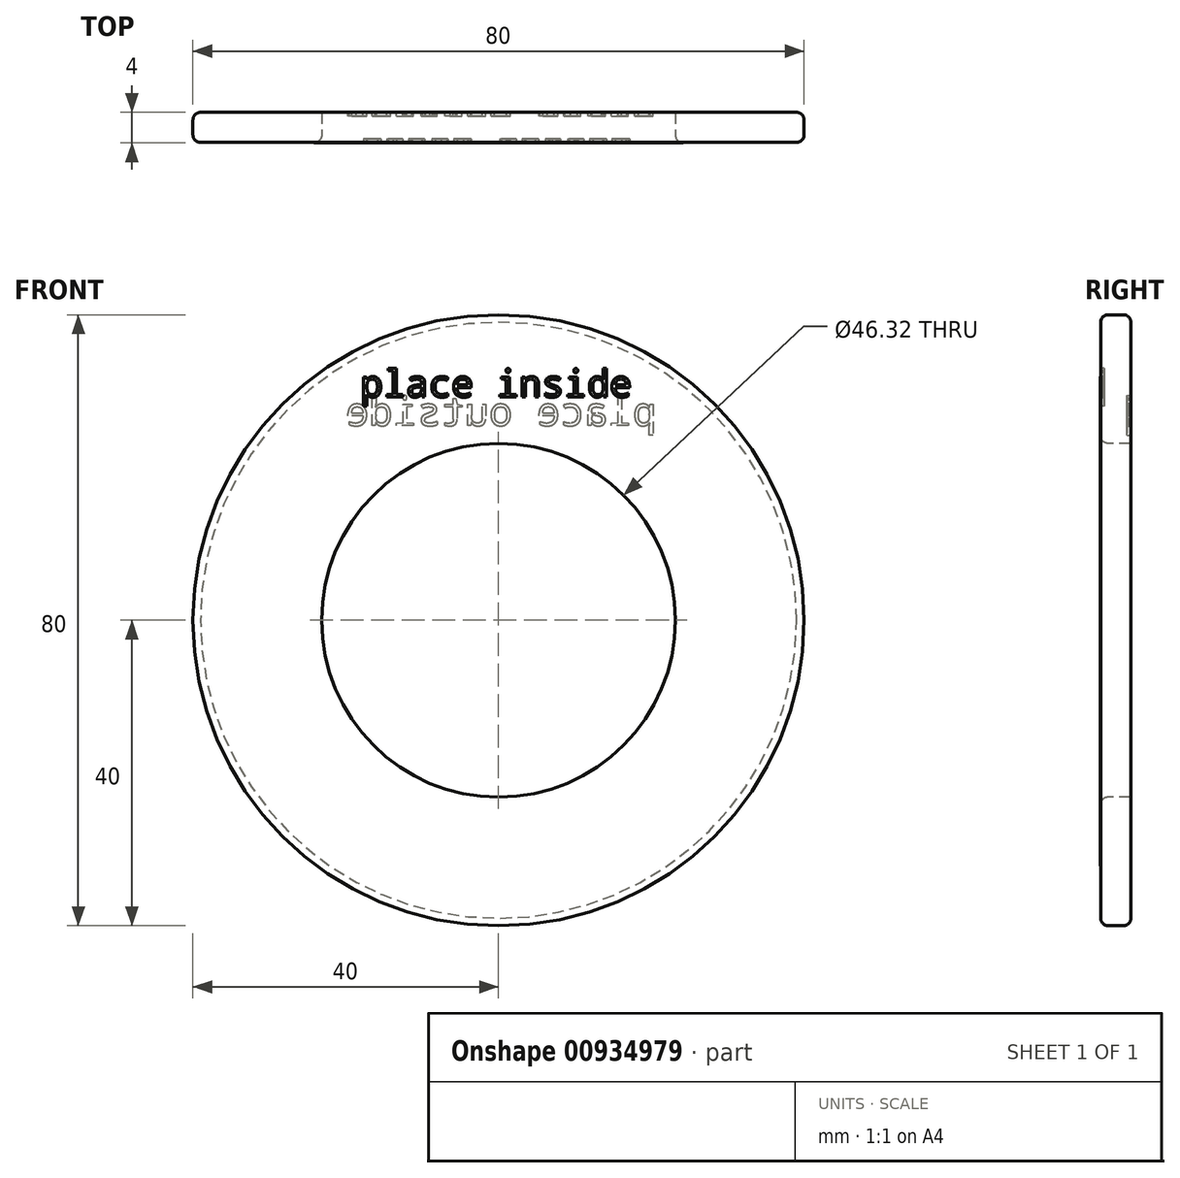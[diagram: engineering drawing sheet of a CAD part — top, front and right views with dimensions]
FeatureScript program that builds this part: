
annotation { "Feature Type Name" : "Feature", "Feature Type Description" : "" }
export const myFeature = defineFeature(function(context is Context, id is Id, definition is map)
    precondition{}
    {
        {
            var Q0;
            Q0=qCreatedBy(makeId("Right.planeOp"),FACE);
            var sketch = newSketch(context, id + "F0", { "sketchPlane" : qUnion([Q0])});
            skLineSegment(sketch, "E0", {"start": v(0, 0) * mm, "end": v(73, 0) * mm, "construction": true});
            skLineSegment(sketch, "E1.bottom", {"start": v(73, 0) * mm, "end": v(69, 0) * mm});
            skPoint(sketch, "E2.orphan", {"position": v(0, 16.15) * mm});
            skLineSegment(sketch, "E3.0", {"start": v(69, 16.15) * mm, "end": v(69, 16.15) * mm});
            skLineSegment(sketch, "E4.0", {"start": v(69, 23.16) * mm, "end": v(73, 23.16) * mm});
            skLineSegment(sketch, "E5", {"start": v(72, 40) * mm, "end": v(70.05, 40) * mm});
            skLineSegment(sketch, "E6", {"start": v(69.05, 39) * mm, "end": v(69, 23.16) * mm});
            skPoint(sketch, "E7.visualSharp", {"position": v(69.05, 40) * mm});
            skArc(sketch, "E7.filletArc", {"start": v(70.05, 40) * mm, "mid": v(69.34, 39.7) * mm, "end": v(69.05, 39) * mm});
            skPoint(sketch, "E8.visualSharp", {"position": v(73, 40) * mm});
            skArc(sketch, "E8.filletArc", {"start": v(73, 39.01) * mm, "mid": v(72.7, 39.71) * mm, "end": v(72, 40) * mm});
            skLineSegment(sketch, "E9", {"start": v(73, 39.01) * mm, "end": v(73, 23.16) * mm});
            skSolve(sketch);
        }
        {
            var Q0;
            Q0=makeQuery(id+"F0.imprint","IMPRINT",FACE,{"disambiguationData":[TD([[makeQuery(id+"F0.imprint","IMPRINT",EDGE,{"derivedFrom":sQuery(id+"F0.wireOp",EDGE,"E4.0")}),1.0]])]});
            var Q1;
            Q1=sQuery(id+"F0.wireOp",EDGE,"E0");
            revolve(context, id + "F1", {"surfaceOperationType" : NewSurfaceOperationType.NEW, "entities" : qUnion([Q0]), "axis" : qUnion([Q1]), "revolveType" : RevolveType.FULL});
        }
        {
            var Q0;
            Q0=makeQuery(id+"F1.opRevolve","SWEPT_EDGE",EDGE,{"disambiguationData":[OSD([sQuery(id+"F0.wireOp",EDGE,"E4.0"),sQuery(id+"F0.wireOp",EDGE,"E6")])]});
            fillet(context, id + "F2", {"entities" : qUnion([Q0]), "radius" : 1 * mm, "tangentPropagation" : true, "allowEdgeOverflow" : false});
        }
        {
            var Q0;
            Q0=qCreatedBy(makeId("Front.planeOp"),FACE);
            var sketch = newSketch(context, id + "F3", { "sketchPlane" : qUnion([Q0])});
            skText(sketch, "E10", { "text": "place inside", "fontName": "DroidSansMono.ttf"});
            const initialGuessF3  = {"E10": [-0.01804, 0.02923, 1, 0, 0.00355]};
            skSetInitialGuess(sketch, initialGuessF3);
            skSolve(sketch);
        }
        {
            var Q0;
            Q0 = qSketchRegion(id + "F3", true);
            extrude(context, id + "F4", {"entities" : qUnion([Q0]), "operationType" : NewBodyOperationType.REMOVE, "endBound" : BoundingType.UP_TO_NEXT, "oppositeDirection" : true, "depth" : 66.4 * mm, "hasOffset" : true, "offsetDistance" : 0.5 * mm, "offsetOppositeDirection" : true, "hasSecondDirection" : true, "secondDirectionBound" : SecondDirectionBoundingType.UP_TO_NEXT, "secondDirectionOppositeDirection" : true, "secondDirectionDepth" : 41.3 * mm});
        }
        {
            var Q0;
            Q0=qCreatedBy(makeId("Front.planeOp"),FACE);
            cPlane(context, id + "F5", {"entities" : qUnion([Q0]), "cplaneType" : CPlaneType.OFFSET, "offset" : 97.9 * mm, "oppositeDirection" : true, "width" : 150 * mm, "height" : 150 * mm});
        }
        {
            var Q0;
            Q0=qCreatedBy(id+"F5.planeOp",FACE);
            var sketch = newSketch(context, id + "F6", { "sketchPlane" : qUnion([Q0])});
            skLineSegment(sketch, "E11", {"start": v(77.57, 0) * mm, "end": v(-72.43, 0) * mm, "construction": true});
            skLineSegment(sketch, "E12", {"start": v(0, 70.28) * mm, "end": v(0, -87.63) * mm, "construction": true});
            skSolve(sketch);
        }
        {
            var Q0;
            Q0=sQuery(id+"F6.wireOp",EDGE,"E12");
            cPlane(context, id + "F7", {"entities" : qUnion([Q0]), "cplaneType" : CPlaneType.LINE_ANGLE, "offset" : 25 * mm, "angle" : 90 * degree, "width" : 150 * mm, "height" : 150 * mm});
        }
        {
            var Q0;
            Q0=qCreatedBy(id+"F7.planeOp",FACE);
            var sketch = newSketch(context, id + "F8", { "sketchPlane" : qUnion([Q0])});
            skText(sketch, "E13", { "text": "place outside", "fontName": "DroidSansMono.ttf"});
            const initialGuessF8  = {"E13": [-0.0206, 0.02548, 1, 0, 0.00375]};
            skSetInitialGuess(sketch, initialGuessF8);
            skSolve(sketch);
        }
        {
            var Q0;
            Q0 = qSketchRegion(id + "F8", true);
            extrude(context, id + "F9", {"entities" : qUnion([Q0]), "operationType" : NewBodyOperationType.REMOVE, "endBound" : BoundingType.UP_TO_NEXT, "oppositeDirection" : true, "depth" : 25 * mm, "hasOffset" : true, "offsetDistance" : 0.5 * mm, "offsetOppositeDirection" : true, "hasSecondDirection" : true, "secondDirectionBound" : SecondDirectionBoundingType.UP_TO_NEXT, "secondDirectionOppositeDirection" : true, "secondDirectionDepth" : 25 * mm});
        }
    });
